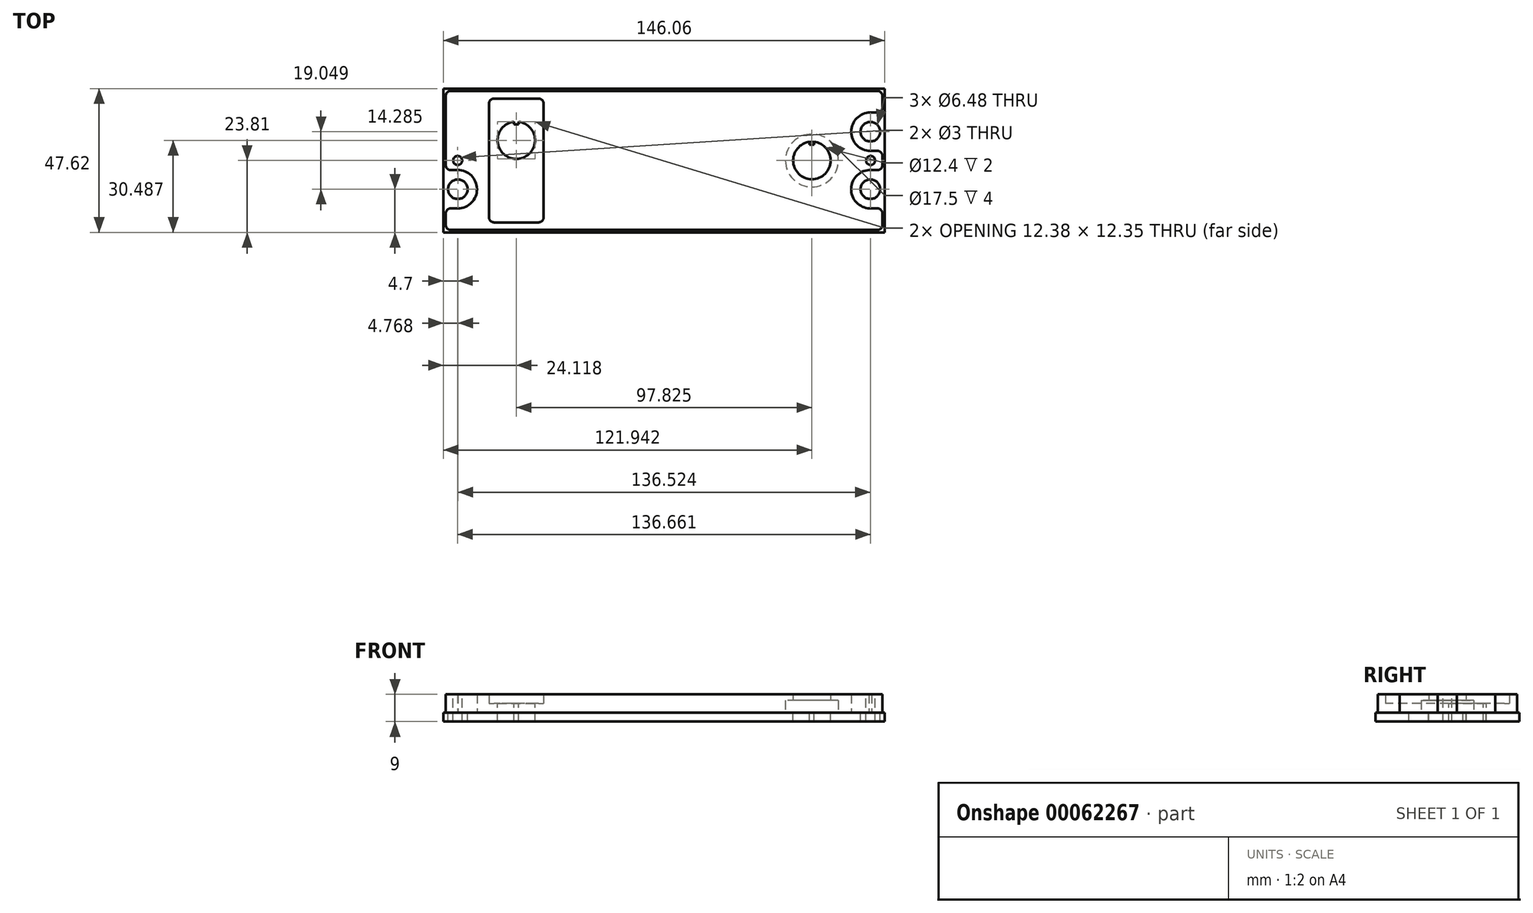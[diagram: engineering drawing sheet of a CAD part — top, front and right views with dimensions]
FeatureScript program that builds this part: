
annotation { "Feature Type Name" : "Feature", "Feature Type Description" : "" }
export const myFeature = defineFeature(function(context is Context, id is Id, definition is map)
    precondition{}
    {
        {
            var Q0;
            Q0=qCreatedBy(makeId("Top.planeOp"),FACE);
            var sketch = newSketch(context, id + "F0", { "sketchPlane" : qUnion([Q0])});
            skLineSegment(sketch, "E0", {"start": v(72.22, -23.01) * mm, "end": v(72.22, -15.86) * mm});
            skLineSegment(sketch, "E1", {"start": v(72.22, -3.19) * mm, "end": v(72.22, 3.17) * mm});
            skLineSegment(sketch, "E2", {"start": v(-68.2, -15.87) * mm, "end": v(-72.23, -15.87) * mm});
            skLineSegment(sketch, "E3", {"start": v(68.26, 15.87) * mm, "end": v(72.22, 15.87) * mm});
            skLineSegment(sketch, "E4", {"start": v(68.26, 3.17) * mm, "end": v(72.22, 3.17) * mm});
            skLineSegment(sketch, "E5", {"start": v(67.83, -3.19) * mm, "end": v(72.22, -3.19) * mm});
            skArc(sketch, "E6", {"start": v(67.83, -3.19) * mm, "mid": v(61.93, -9.96) * mm, "end": v(68.7, -15.86) * mm});
            skLineSegment(sketch, "E7", {"start": v(68.7, -15.86) * mm, "end": v(72.22, -15.86) * mm});
            skLineSegment(sketch, "E8", {"start": v(-68.33, -3.17) * mm, "end": v(-72.23, -3.17) * mm});
            skArc(sketch, "E9", {"start": v(68.26, 15.87) * mm, "mid": v(61.91, 9.52) * mm, "end": v(68.26, 3.17) * mm});
            skLineSegment(sketch, "E10", {"start": v(72.22, 15.87) * mm, "end": v(72.22, 23.01) * mm});
            skLineSegment(sketch, "E11", {"start": v(-72.23, -3.17) * mm, "end": v(-72.23, 3.17) * mm});
            skLineSegment(sketch, "E12", {"start": v(-72.23, 15.87) * mm, "end": v(-72.23, 23.01) * mm});
            skLineSegment(sketch, "E13", {"start": v(72.22, -23.01) * mm, "end": v(-72.23, -23.01) * mm});
            skLineSegment(sketch, "E14", {"start": v(-72.23, 23.01) * mm, "end": v(72.23, 23.01) * mm});
            skArc(sketch, "E15", {"start": v(-68.2, -15.87) * mm, "mid": v(-61.91, -9.46) * mm, "end": v(-68.33, -3.17) * mm});
            skLineSegment(sketch, "E16", {"start": v(-72.23, -23.01) * mm, "end": v(-72.23, -15.87) * mm});
            skCircle(sketch, "E17", {"center": v(68.26, -9.52) * mm, "radius": 3.24 * mm});
            skLineSegment(sketch, "E18", {"start": v(-73.03, -23.81) * mm, "end": v(-73.03, 23.81) * mm});
            skCircle(sketch, "E19", {"center": v(-68.26, -9.52) * mm, "radius": 3.24 * mm});
            skLineSegment(sketch, "E20", {"start": v(73.03, -23.81) * mm, "end": v(73.03, 23.81) * mm});
            skLineSegment(sketch, "E21", {"start": v(-73.03, 23.81) * mm, "end": v(73.03, 23.81) * mm});
            skLineSegment(sketch, "E22", {"start": v(73.03, -23.81) * mm, "end": v(-73.03, -23.81) * mm});
            skCircle(sketch, "E23", {"center": v(68.26, 9.52) * mm, "radius": 3.24 * mm});
            skLineSegment(sketch, "E24", {"start": v(-72.23, 3.17) * mm, "end": v(-72.23, 15.87) * mm});
            skCircle(sketch, "E25", {"center": v(-68.33, 0) * mm, "radius": 1.5 * mm});
            skCircle(sketch, "E26.MirrorC", {"center": v(68.33, 0) * mm, "radius": 1.5 * mm});
            skSolve(sketch);
        }
        {
            var Q0;
            Q0 = qSketchRegion(id + "F0", true);
            var Q1;
            Q1=makeQuery(id+"F0.imprint","IMPRINT",FACE,{"disambiguationData":[TD([[makeQuery(id+"F0.imprint","IMPRINT",EDGE,{"derivedFrom":sQuery(id+"F0.wireOp",EDGE,"E0")}),1.0]])]});
            extrude(context, id + "F1", {"entities" : qUnion([Q0, Q1]), "oppositeDirection" : true, "depth" : 3 * mm});
        }
        {
            var Q0;
            Q0=makeQuery(id+"F0.imprint","IMPRINT",FACE,{"disambiguationData":[TD([[makeQuery(id+"F0.imprint","IMPRINT",EDGE,{"derivedFrom":sQuery(id+"F0.wireOp",EDGE,"E0")}),1.0]])]});
            var sketch = newSketch(context, id + "F2", { "sketchPlane" : qUnion([Q0])});
            skLineSegment(sketch, "E27.bottom", {"start": v(-39.91, 20.5) * mm, "end": v(-57.91, 20.5) * mm});
            skLineSegment(sketch, "E27.top", {"start": v(-39.91, -20.5) * mm, "end": v(-57.91, -20.5) * mm});
            skLineSegment(sketch, "E27.left", {"start": v(-39.91, 20.5) * mm, "end": v(-39.91, -20.5) * mm});
            skLineSegment(sketch, "E27.right", {"start": v(-57.91, 20.5) * mm, "end": v(-57.91, -20.5) * mm});
            skPoint(sketch, "E27.middle", {"position": v(-48.91, 0) * mm});
            skCircle(sketch, "E28", {"center": v(-48.91, 6.7) * mm, "radius": 6.2 * mm});
            skLineSegment(sketch, "E29.bottom", {"start": v(-48.16, 11.9) * mm, "end": v(-49.66, 11.9) * mm});
            skLineSegment(sketch, "E29.top", {"start": v(-48.16, 13.9) * mm, "end": v(-49.66, 13.9) * mm});
            skLineSegment(sketch, "E29.left", {"start": v(-48.16, 11.9) * mm, "end": v(-48.16, 13.9) * mm});
            skLineSegment(sketch, "E29.right", {"start": v(-49.66, 11.9) * mm, "end": v(-49.66, 13.9) * mm});
            skPoint(sketch, "E29.middle", {"position": v(-48.91, 12.9) * mm});
            skCircle(sketch, "E30", {"center": v(48.91, 0) * mm, "radius": 6.2 * mm});
            skLineSegment(sketch, "E31.bottom", {"start": v(49.66, 5.2) * mm, "end": v(48.16, 5.2) * mm});
            skLineSegment(sketch, "E31.top", {"start": v(49.66, 7.2) * mm, "end": v(48.16, 7.2) * mm});
            skLineSegment(sketch, "E31.left", {"start": v(49.66, 5.2) * mm, "end": v(49.66, 7.2) * mm});
            skLineSegment(sketch, "E31.right", {"start": v(48.16, 5.2) * mm, "end": v(48.16, 7.2) * mm});
            skPoint(sketch, "E31.middle", {"position": v(48.91, 6.2) * mm});
            skSolve(sketch);
        }
        {
            var Q0;
            {var subQ5=sQuery(id+"F2.wireOp",EDGE,"E29.bottom");Q0=makeQuery(id+"F2.imprint","IMPRINT",FACE,{"disambiguationData":[TD([[makeQuery(id+"F2.imprint","IMPRINT",EDGE,{"derivedFrom":subQ5}),1.0]])]});}
            var Q1;
            {var subQ5=sQuery(id+"F2.wireOp",EDGE,"E31.bottom");Q1=makeQuery(id+"F2.imprint","IMPRINT",FACE,{"disambiguationData":[TD([[makeQuery(id+"F2.imprint","IMPRINT",EDGE,{"derivedFrom":subQ5}),1.0]])]});}
            extrude(context, id + "F3", {"entities" : qUnion([Q0, Q1]), "operationType" : NewBodyOperationType.REMOVE, "oppositeDirection" : true, "depth" : 25 * mm});
        }
        {
            var Q0;
            Q0=makeQuery(id+"F2.imprint","IMPRINT",FACE,{"disambiguationData":[TD([[makeQuery(id+"F2.imprint","IMPRINT",EDGE,{"derivedFrom":sQuery(id+"F2.wireOp",EDGE,"E27.bottom")}),-1.0]])]});
            var Q1;
            {var subQ5=sQuery(id+"F2.wireOp",EDGE,"E31.top");Q1=makeQuery(id+"F2.imprint","IMPRINT",FACE,{"disambiguationData":[TD([[makeQuery(id+"F2.imprint","IMPRINT",EDGE,{"derivedFrom":subQ5}),1.0]])]});}
            extrude(context, id + "F4", {"entities" : qUnion([Q0, Q1]), "depth" : 6 * mm});
        }
        {
            var Q0;
            Q0=makeQuery(id+"F4.opExtrude","SWEPT_EDGE",EDGE,{"disambiguationData":[OSD([sQuery(id+"F0.wireOp",EDGE,"E16"),sQuery(id+"F0.wireOp",EDGE,"E13")])]});
            var Q1;
            Q1=makeQuery(id+"F4.opExtrude","SWEPT_EDGE",EDGE,{"disambiguationData":[OSD([sQuery(id+"F0.wireOp",EDGE,"E16"),sQuery(id+"F0.wireOp",EDGE,"E2")])]});
            var Q2;
            Q2=makeQuery(id+"F4.opExtrude","SWEPT_EDGE",EDGE,{"disambiguationData":[OSD([sQuery(id+"F0.wireOp",EDGE,"E11"),sQuery(id+"F0.wireOp",EDGE,"E8")])]});
            var Q3;
            Q3=makeQuery(id+"F4.opExtrude","SWEPT_EDGE",EDGE,{"disambiguationData":[OSD([sQuery(id+"F0.wireOp",EDGE,"E14"),sQuery(id+"F0.wireOp",EDGE,"E12")])]});
            var Q4;
            Q4=makeQuery(id+"F4.opExtrude","SWEPT_EDGE",EDGE,{"disambiguationData":[OSD([sQuery(id+"F0.wireOp",EDGE,"E0"),sQuery(id+"F0.wireOp",EDGE,"E13")])]});
            var Q5;
            Q5=makeQuery(id+"F4.opExtrude","SWEPT_EDGE",EDGE,{"disambiguationData":[OSD([sQuery(id+"F0.wireOp",EDGE,"E0"),sQuery(id+"F0.wireOp",EDGE,"E7")])]});
            var Q6;
            Q6=makeQuery(id+"F4.opExtrude","SWEPT_EDGE",EDGE,{"disambiguationData":[OSD([sQuery(id+"F0.wireOp",EDGE,"E5"),sQuery(id+"F0.wireOp",EDGE,"E1")])]});
            var Q7;
            Q7=makeQuery(id+"F4.opExtrude","SWEPT_EDGE",EDGE,{"disambiguationData":[OSD([sQuery(id+"F0.wireOp",EDGE,"E1"),sQuery(id+"F0.wireOp",EDGE,"E4")])]});
            var Q8;
            Q8=makeQuery(id+"F4.opExtrude","SWEPT_EDGE",EDGE,{"disambiguationData":[OSD([sQuery(id+"F0.wireOp",EDGE,"E3"),sQuery(id+"F0.wireOp",EDGE,"E10")])]});
            var Q9;
            Q9=makeQuery(id+"F4.opExtrude","SWEPT_EDGE",EDGE,{"disambiguationData":[OSD([sQuery(id+"F0.wireOp",EDGE,"E14"),sQuery(id+"F0.wireOp",EDGE,"E10")])]});
            var Q10;
            Q10=makeQuery(id+"F4.opExtrude","SWEPT_EDGE",EDGE,{"disambiguationData":[OSD([sQuery(id+"F2.wireOp",EDGE,"E27.bottom"),sQuery(id+"F2.wireOp",EDGE,"E27.right")])]});
            var Q11;
            Q11=makeQuery(id+"F4.opExtrude","SWEPT_EDGE",EDGE,{"disambiguationData":[OSD([sQuery(id+"F2.wireOp",EDGE,"E27.bottom"),sQuery(id+"F2.wireOp",EDGE,"E27.left")])]});
            var Q12;
            Q12=makeQuery(id+"F4.opExtrude","SWEPT_EDGE",EDGE,{"disambiguationData":[OSD([sQuery(id+"F2.wireOp",EDGE,"E27.top"),sQuery(id+"F2.wireOp",EDGE,"E27.left")])]});
            var Q13;
            Q13=makeQuery(id+"F4.opExtrude","SWEPT_EDGE",EDGE,{"disambiguationData":[OSD([sQuery(id+"F2.wireOp",EDGE,"E27.top"),sQuery(id+"F2.wireOp",EDGE,"E27.right")])]});
            fillet(context, id + "F5", {"entities" : qUnion([Q0, Q1, Q2, Q3, Q4, Q5, Q6, Q7, Q8, Q9, Q10, Q11, Q12, Q13]), "radius" : 1.59 * mm, "tangentPropagation" : true, "allowEdgeOverflow" : false});
        }
        {
            var Q0;
            Q0=makeQuery(id+"F4.opExtrude","CAP_FACE",FACE,{"disambiguationData":[OSD([sQuery(id+"F0.wireOp",EDGE,"E0"),sQuery(id+"F0.wireOp",EDGE,"E14"),sQuery(id+"F0.wireOp",EDGE,"E9"),sQuery(id+"F0.wireOp",EDGE,"E16"),sQuery(id+"F0.wireOp",EDGE,"E2"),sQuery(id+"F0.wireOp",EDGE,"E5"),sQuery(id+"F0.wireOp",EDGE,"E12"),sQuery(id+"F0.wireOp",EDGE,"E13"),sQuery(id+"F0.wireOp",EDGE,"E3"),sQuery(id+"F0.wireOp",EDGE,"E11"),sQuery(id+"F0.wireOp",EDGE,"E10"),sQuery(id+"F0.wireOp",EDGE,"E15"),sQuery(id+"F0.wireOp",EDGE,"E1"),sQuery(id+"F0.wireOp",EDGE,"E6"),sQuery(id+"F0.wireOp",EDGE,"E7"),sQuery(id+"F0.wireOp",EDGE,"E8"),sQuery(id+"F0.wireOp",EDGE,"E4"),sQuery(id+"F0.wireOp",EDGE,"E24"),sQuery(id+"F2.wireOp",EDGE,"E27.bottom"),sQuery(id+"F2.wireOp",EDGE,"E27.top"),sQuery(id+"F2.wireOp",EDGE,"E27.left"),sQuery(id+"F2.wireOp",EDGE,"E27.right")])],"isStart":false});
            var sketch = newSketch(context, id + "F6", { "sketchPlane" : qUnion([Q0])});
            skCircle(sketch, "E32", {"center": v(-68.33, 0) * mm, "radius": 1.5 * mm});
            skCircle(sketch, "E33.MirrorC", {"center": v(68.33, 0) * mm, "radius": 1.5 * mm});
            skSolve(sketch);
        }
        {
            var Q0;
            Q0 = qSketchRegion(id + "F6", true);
            extrude(context, id + "F7", {"entities" : qUnion([Q0]), "operationType" : NewBodyOperationType.REMOVE, "endBound" : BoundingType.THROUGH_ALL, "oppositeDirection" : true, "depth" : 25 * mm});
        }
        {
            var Q0;
            Q0=makeQuery(id+"F0.imprint","IMPRINT",FACE,{"disambiguationData":[TD([[makeQuery(id+"F0.imprint","IMPRINT",EDGE,{"derivedFrom":sQuery(id+"F0.wireOp",EDGE,"E0")}),1.0]])]});
            var sketch = newSketch(context, id + "F8", { "sketchPlane" : qUnion([Q0])});
            skCircle(sketch, "E34", {"center": v(48.91, 0) * mm, "radius": 8.75 * mm});
            skSolve(sketch);
        }
        {
            var Q0;
            Q0 = qSketchRegion(id + "F8", true);
            extrude(context, id + "F9", {"entities" : qUnion([Q0]), "operationType" : NewBodyOperationType.REMOVE, "depth" : 4 * mm});
        }
        {
            var Q0;
            Q0=makeQuery(id+"F2.imprint","IMPRINT",FACE,{"disambiguationData":[TD([[makeQuery(id+"F2.imprint","IMPRINT",EDGE,{"derivedFrom":sQuery(id+"F2.wireOp",EDGE,"E27.bottom")}),-1.0]])]});
            var sketch = newSketch(context, id + "F10", { "sketchPlane" : qUnion([Q0])});
            skCircle(sketch, "E35", {"center": v(-48.91, 6.7) * mm, "radius": 6.2 * mm});
            skLineSegment(sketch, "E36.bottom", {"start": v(-48.16, 11.9) * mm, "end": v(-49.66, 11.9) * mm});
            skLineSegment(sketch, "E36.top", {"start": v(-48.16, 13.9) * mm, "end": v(-49.66, 13.9) * mm});
            skLineSegment(sketch, "E36.left", {"start": v(-48.16, 11.9) * mm, "end": v(-48.16, 13.9) * mm});
            skLineSegment(sketch, "E36.right", {"start": v(-49.66, 11.9) * mm, "end": v(-49.66, 13.9) * mm});
            skPoint(sketch, "E36.middle", {"position": v(-48.91, 12.9) * mm});
            skSolve(sketch);
        }
        {
            var Q0;
            Q0=makeQuery(id+"F2.imprint","IMPRINT",FACE,{"disambiguationData":[TD([[makeQuery(id+"F2.imprint","IMPRINT",EDGE,{"derivedFrom":sQuery(id+"F2.wireOp",EDGE,"E27.bottom")}),1.0]])]});
            var Q1;
            {var subQ5=sQuery(id+"F10.wireOp",EDGE,"E36.top");Q1=makeQuery(id+"F10.imprint","IMPRINT",FACE,{"disambiguationData":[TD([[makeQuery(id+"F10.imprint","IMPRINT",EDGE,{"derivedFrom":subQ5}),1.0]])]});}
            var Q2;
            {var subQ5=sQuery(id+"F10.wireOp",EDGE,"E36.bottom");Q2=makeQuery(id+"F10.imprint","IMPRINT",FACE,{"disambiguationData":[TD([[makeQuery(id+"F10.imprint","IMPRINT",EDGE,{"derivedFrom":subQ5}),-1.0]])]});}
            extrude(context, id + "F11", {"entities" : qUnion([Q0, Q1, Q2]), "operationType" : NewBodyOperationType.ADD, "depth" : 3 * mm});
        }
    });
